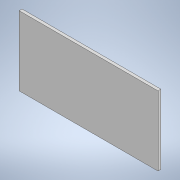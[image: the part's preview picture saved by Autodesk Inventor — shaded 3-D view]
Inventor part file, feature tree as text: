
AUTODESK INVENTOR PART (.ipt)
format: ipt  version: 2021 (Build 250183000, 183)  size: 94,720 bytes
history: native  units: in
note: dims shown in document units (in); Inventor stores cm internally (conversion verified against a paired STEP export)
features: extrude x1, sketch x1
ambient origin geometry x8: Origin, YZ Plane, XZ Plane, XY Plane, X Axis, Y Axis, Z Axis, Center Point
bodies: Solid1 (feature_tree)
feature tree (2):
  extrude  "Extrusion1"  Depth=1.5in
  sketch  "Sketch1"  dims[d0=3.0in d1=1.5in d2=0.0625in d3=0.0in]
